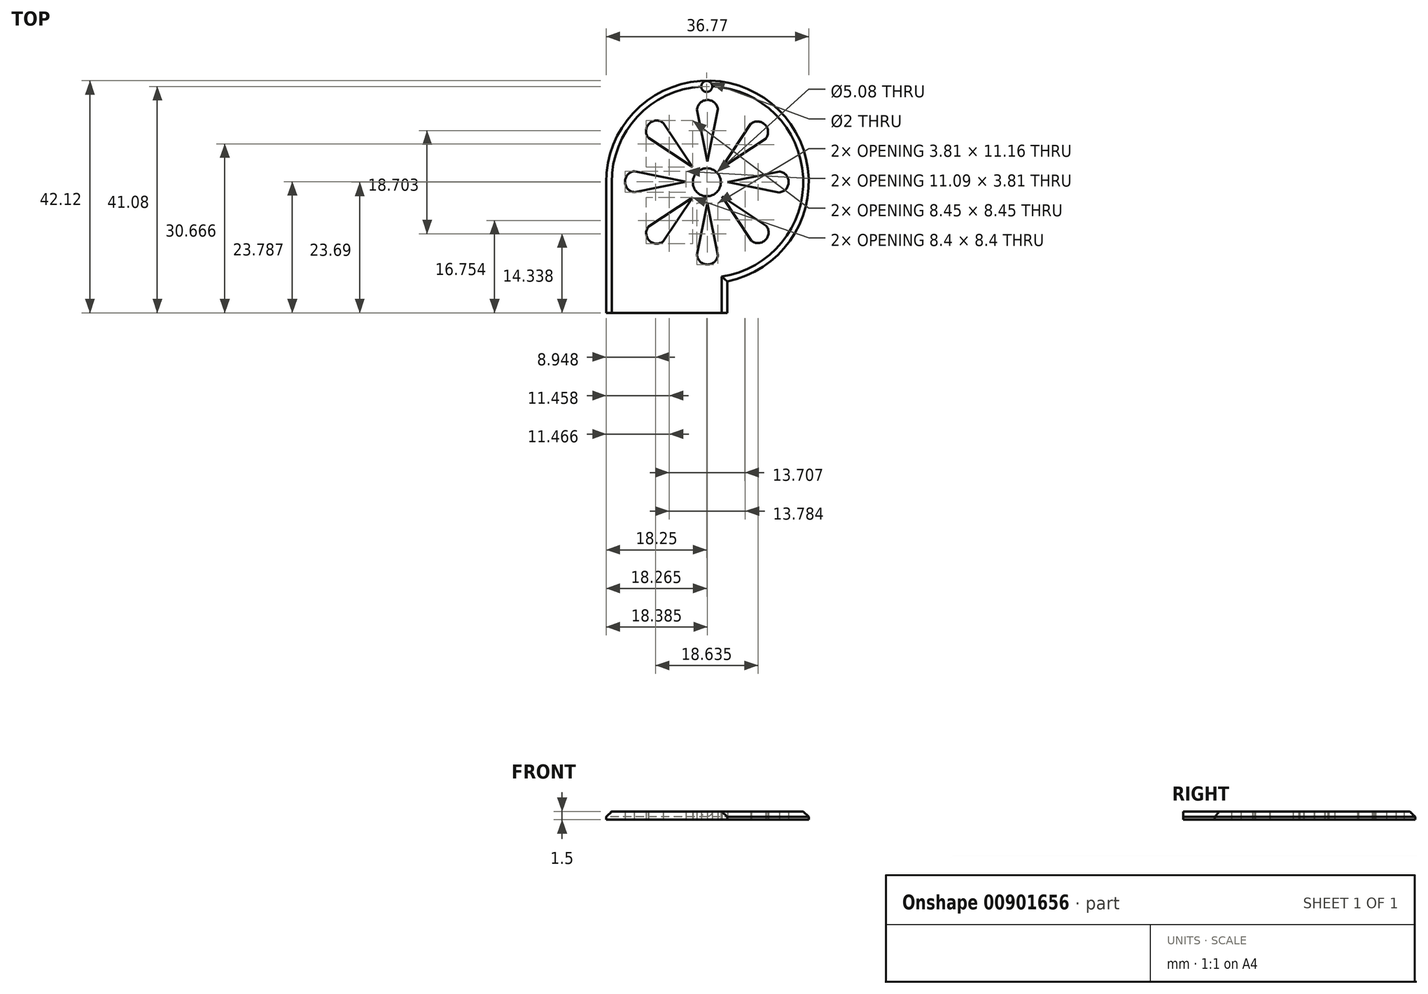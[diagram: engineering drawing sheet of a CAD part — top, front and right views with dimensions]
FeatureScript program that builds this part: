
annotation { "Feature Type Name" : "Feature", "Feature Type Description" : "" }
export const myFeature = defineFeature(function(context is Context, id is Id, definition is map)
    precondition{}
    {
        {
            var Q0;
            Q0=qCreatedBy(makeId("Top.planeOp"),FACE);
            var sketch = newSketch(context, id + "F0", { "sketchPlane" : qUnion([Q0])});
            skCircle(sketch, "E0", {"center": v(0.24, 0.05) * mm, "radius": 18.38 * mm});
            skLineSegment(sketch, "E1", {"start": v(-15.18, -23.69) * mm, "end": v(1.28, -23.69) * mm});
            skLineSegment(sketch, "E2", {"start": v(-18.14, -0.06) * mm, "end": v(-18.14, -23.69) * mm});
            skLineSegment(sketch, "E3", {"start": v(-18.14, -23.69) * mm, "end": v(-15.18, -23.69) * mm});
            skLineSegment(sketch, "E4", {"start": v(3.83, -18.4) * mm, "end": v(3.83, -23.69) * mm});
            skLineSegment(sketch, "E5", {"start": v(3.83, -23.69) * mm, "end": v(1.96, -23.69) * mm});
            skCircle(sketch, "E6", {"center": v(0.12, 0) * mm, "radius": 2.54 * mm});
            skCircle(sketch, "E7", {"center": v(0.11, 17.39) * mm, "radius": 1 * mm});
            skLineSegment(sketch, "E8", {"start": v(0.24, 0.05) * mm, "end": v(1.6, 0.05) * mm});
            skLineSegment(sketch, "E9", {"start": v(0.24, 0.05) * mm, "end": v(5.35, 2.16) * mm, "construction": true});
            skLineSegment(sketch, "E10", {"start": v(0.24, 0.05) * mm, "end": v(2.55, 0.5) * mm});
            skLineSegment(sketch, "E11", {"start": v(0.24, 3.77) * mm, "end": v(0.24, 13.23) * mm});
            skLineSegment(sketch, "E12", {"start": v(0.24, 3.77) * mm, "end": v(2.15, 13.23) * mm});
            skLineSegment(sketch, "E13.MirrorCS", {"start": v(0.24, 3.77) * mm, "end": v(-1.66, 13.23) * mm});
            skArc(sketch, "E14", {"start": v(2.15, 13.23) * mm, "mid": v(0.24, 14.93) * mm, "end": v(-1.66, 13.23) * mm});
            skArc(sketch, "E15.MirrorCS", {"start": v(2.15, -13.23) * mm, "mid": v(0.24, -14.93) * mm, "end": v(-1.66, -13.23) * mm});
            skLineSegment(sketch, "E16.MirrorCS", {"start": v(0.24, -3.77) * mm, "end": v(2.15, -13.23) * mm});
            skLineSegment(sketch, "E17.MirrorCS", {"start": v(0.24, -3.77) * mm, "end": v(-1.66, -13.23) * mm});
            skArc(sketch, "E18.MirrorCS", {"start": v(-13.03, 2) * mm, "mid": v(-14.73, 0.1) * mm, "end": v(-13.03, -1.8) * mm});
            skLineSegment(sketch, "E19.MirrorCS", {"start": v(-3.65, 0.1) * mm, "end": v(-13.03, -1.8) * mm});
            skLineSegment(sketch, "E20.MirrorCS", {"start": v(-3.65, 0.1) * mm, "end": v(-13.03, 2) * mm});
            skArc(sketch, "E21.MirrorCS", {"start": v(13.28, 1.96) * mm, "mid": v(14.99, 0.06) * mm, "end": v(13.28, -1.85) * mm});
            skLineSegment(sketch, "E22.MirrorCS", {"start": v(3.9, 0.06) * mm, "end": v(13.28, 1.96) * mm});
            skLineSegment(sketch, "E23.MirrorCS", {"start": v(3.9, 0.06) * mm, "end": v(13.28, -1.85) * mm});
            skArc(sketch, "E24.MirrorCS", {"start": v(-7.8, 10.78) * mm, "mid": v(-10.35, 10.64) * mm, "end": v(-10.49, 8.09) * mm});
            skLineSegment(sketch, "E25.MirrorCS", {"start": v(-2.46, 2.75) * mm, "end": v(-7.8, 10.78) * mm});
            skLineSegment(sketch, "E26.MirrorCS", {"start": v(-2.46, 2.75) * mm, "end": v(-10.49, 8.09) * mm});
            skLineSegment(sketch, "E27.MirrorCS", {"start": v(-2.47, -2.74) * mm, "end": v(-10.46, -8.02) * mm});
            skArc(sketch, "E28.MirrorCS", {"start": v(-7.76, -10.72) * mm, "mid": v(-10.31, -10.58) * mm, "end": v(-10.46, -8.02) * mm});
            skLineSegment(sketch, "E29.MirrorCS", {"start": v(-2.47, -2.74) * mm, "end": v(-7.76, -10.72) * mm});
            skArc(sketch, "E30.MirrorCS", {"start": v(10.9, -7.92) * mm, "mid": v(10.77, -10.47) * mm, "end": v(8.21, -10.61) * mm});
            skLineSegment(sketch, "E31.MirrorCS", {"start": v(2.88, -2.58) * mm, "end": v(8.21, -10.61) * mm});
            skLineSegment(sketch, "E32.MirrorCS", {"start": v(2.88, -2.58) * mm, "end": v(10.9, -7.92) * mm});
            skArc(sketch, "E33.MirrorCS", {"start": v(10.81, 7.92) * mm, "mid": v(10.67, 10.47) * mm, "end": v(8.12, 10.6) * mm});
            skLineSegment(sketch, "E34.MirrorCS", {"start": v(2.83, 2.63) * mm, "end": v(10.81, 7.92) * mm});
            skLineSegment(sketch, "E35.MirrorCS", {"start": v(2.83, 2.63) * mm, "end": v(8.12, 10.6) * mm});
            skLineSegment(sketch, "E36", {"start": v(-3.65, 0.1) * mm, "end": v(-2.41, 0.1) * mm, "construction": true});
            skLineSegment(sketch, "E37", {"start": v(-2.47, -2.74) * mm, "end": v(-1.6, -1.86) * mm, "construction": true});
            skLineSegment(sketch, "E38", {"start": v(0.24, -3.77) * mm, "end": v(0.24, -2.54) * mm, "construction": true});
            skLineSegment(sketch, "E39", {"start": v(3.9, 0.06) * mm, "end": v(2.66, 0.06) * mm, "construction": true});
            skLineSegment(sketch, "E40", {"start": v(2.88, -2.58) * mm, "end": v(2.88, -1.8) * mm, "construction": true});
            skLineSegment(sketch, "E41", {"start": v(2.88, -2.58) * mm, "end": v(2, -1.7) * mm, "construction": true});
            skLineSegment(sketch, "E42", {"start": v(0.24, 3.77) * mm, "end": v(0.24, 2.54) * mm, "construction": true});
            skLineSegment(sketch, "E43", {"start": v(2.83, 2.63) * mm, "end": v(1.96, 1.76) * mm, "construction": true});
            skLineSegment(sketch, "E44", {"start": v(2.83, 2.63) * mm, "end": v(2.16, 2.63) * mm, "construction": true});
            skLineSegment(sketch, "E45", {"start": v(-2.46, 2.75) * mm, "end": v(-2.46, 2.26) * mm, "construction": true});
            skLineSegment(sketch, "E46", {"start": v(-2.46, 2.75) * mm, "end": v(-1.58, 1.88) * mm, "construction": true});
            skLineSegment(sketch, "E47", {"start": v(1.96, -23.69) * mm, "end": v(1.28, -23.69) * mm});
            skLineSegment(sketch, "E48", {"start": v(3.83, -18.4) * mm, "end": v(3.83, -17.98) * mm});
            skSolve(sketch);
        }
        {
            var Q0;
            Q0=makeQuery(id+"F0.imprint","IMPRINT",FACE,{"disambiguationData":[TD([[makeQuery(id+"F0.imprint","IMPRINT",EDGE,{"derivedFrom":sQuery(id+"F0.wireOp",EDGE,"E6")}),-1.0]])]});
            var Q1;
            Q1=makeQuery(id+"F0.imprint","IMPRINT",FACE,{"disambiguationData":[TD([[makeQuery(id+"F0.imprint","IMPRINT",EDGE,{"derivedFrom":sQuery(id+"F0.wireOp",EDGE,"E1")}),1.0]])]});
            extrude(context, id + "F1", {"entities" : qUnion([Q0, Q1]), "depth" : 1.5 * mm, "offsetDistance" : 25.4 * mm});
        }
        {
            var Q0;
            Q0=makeQuery(id+"F1.opExtrude","CAP_EDGE",EDGE,{"disambiguationData":[OSD([sQuery(id+"F0.wireOp",EDGE,"E2")])],"isStart":false});
            var Q1;
            Q1=makeQuery(id+"F1.opExtrude","CAP_EDGE",EDGE,{"disambiguationData":[OSD([sQuery(id+"F0.wireOp",EDGE,"E0")])],"isStart":false});
            var Q2;
            Q2=makeQuery(id+"F1.opExtrude","CAP_EDGE",EDGE,{"disambiguationData":[OSD([sQuery(id+"F0.wireOp",EDGE,"E4")])],"isStart":false});
            chamfer(context, id + "F2", {"entities" : qUnion([Q0, Q1, Q2]), "width" : 1 * mm, "tangentPropagation" : true});
        }
    });
